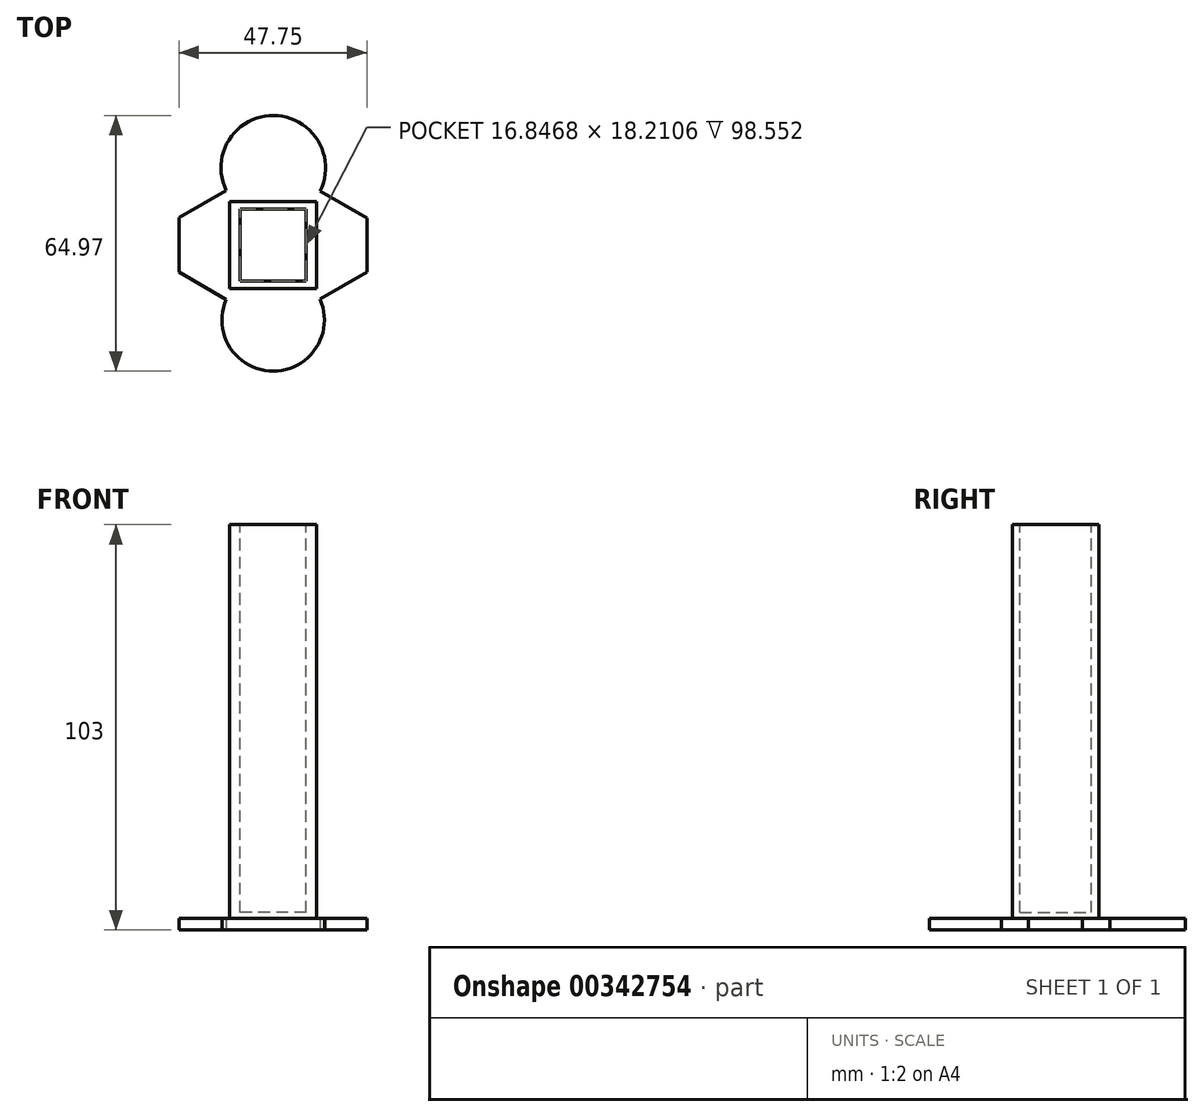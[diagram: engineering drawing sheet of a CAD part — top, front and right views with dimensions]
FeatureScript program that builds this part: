
annotation { "Feature Type Name" : "Feature", "Feature Type Description" : "" }
export const myFeature = defineFeature(function(context is Context, id is Id, definition is map)
    precondition{}
    {
        {
            var Q0;
            Q0=qCreatedBy(makeId("Top.planeOp"),FACE);
            var sketch = newSketch(context, id + "F0", { "sketchPlane" : qUnion([Q0])});
            skCircle(sketch, "E0.cCircle", {"center": v(0, 0) * mm, "radius": 10.33 * mm, "construction": true});
            skLineSegment(sketch, "E0.0", {"start": v(11.92, -0.02) * mm, "end": v(5.94, -10.34) * mm});
            skLineSegment(sketch, "E0.1", {"start": v(5.94, -10.34) * mm, "end": v(-5.98, -10.32) * mm});
            skLineSegment(sketch, "E0.2", {"start": v(-5.98, -10.32) * mm, "end": v(-11.92, 0.02) * mm});
            skLineSegment(sketch, "E0.3", {"start": v(-11.92, 0.02) * mm, "end": v(-5.94, 10.34) * mm});
            skLineSegment(sketch, "E0.4", {"start": v(-5.94, 10.34) * mm, "end": v(5.98, 10.32) * mm});
            skLineSegment(sketch, "E0.5", {"start": v(5.98, 10.32) * mm, "end": v(11.92, -0.02) * mm});
            skPoint(sketch, "E0.0.midPoint", {"position": v(8.93, -5.18) * mm});
            skCircle(sketch, "E1.cCircle", {"center": v(-11.92, 0.02) * mm, "radius": 12 * mm, "construction": true});
            skLineSegment(sketch, "E1.0", {"start": v(-23.93, -6.9) * mm, "end": v(-23.93, 6.95) * mm});
            skLineSegment(sketch, "E1.1", {"start": v(-23.93, 6.95) * mm, "end": v(-11.92, 13.88) * mm});
            skLineSegment(sketch, "E1.2", {"start": v(-11.92, 13.88) * mm, "end": v(0.08, 6.95) * mm});
            skLineSegment(sketch, "E1.3", {"start": v(0.08, 6.95) * mm, "end": v(0.08, -6.9) * mm});
            skLineSegment(sketch, "E1.4", {"start": v(0.08, -6.9) * mm, "end": v(-11.92, -13.84) * mm});
            skLineSegment(sketch, "E1.5", {"start": v(-11.92, -13.84) * mm, "end": v(-23.93, -6.9) * mm});
            skPoint(sketch, "E1.0.midPoint", {"position": v(-23.93, 0.02) * mm});
            skCircle(sketch, "E2.cCircle", {"center": v(11.92, -0.02) * mm, "radius": 11.9 * mm, "construction": true});
            skLineSegment(sketch, "E2.0", {"start": v(23.82, 6.85) * mm, "end": v(23.82, -6.9) * mm});
            skLineSegment(sketch, "E2.1", {"start": v(23.82, -6.9) * mm, "end": v(11.92, -13.76) * mm});
            skLineSegment(sketch, "E2.2", {"start": v(11.92, -13.76) * mm, "end": v(0.02, -6.9) * mm});
            skLineSegment(sketch, "E2.3", {"start": v(0.02, -6.9) * mm, "end": v(0.02, 6.85) * mm});
            skLineSegment(sketch, "E2.4", {"start": v(0.02, 6.85) * mm, "end": v(11.92, 13.72) * mm});
            skLineSegment(sketch, "E2.5", {"start": v(11.92, 13.72) * mm, "end": v(23.82, 6.85) * mm});
            skPoint(sketch, "E2.0.midPoint", {"position": v(23.82, -0.02) * mm});
            skCircle(sketch, "E3.cCircle", {"center": v(0.08, 6.95) * mm, "radius": 6.95 * mm, "construction": true});
            skLineSegment(sketch, "E3.0", {"start": v(4.01, -0.05) * mm, "end": v(-4.01, 0.05) * mm});
            skLineSegment(sketch, "E3.1", {"start": v(-4.01, 0.05) * mm, "end": v(-7.95, 7.04) * mm});
            skLineSegment(sketch, "E3.2", {"start": v(-7.95, 7.04) * mm, "end": v(-3.85, 13.95) * mm});
            skLineSegment(sketch, "E3.3", {"start": v(-3.85, 13.95) * mm, "end": v(4.17, 13.85) * mm});
            skLineSegment(sketch, "E3.4", {"start": v(4.17, 13.85) * mm, "end": v(8.1, 6.86) * mm});
            skLineSegment(sketch, "E3.5", {"start": v(8.1, 6.86) * mm, "end": v(4.01, -0.05) * mm});
            skCircle(sketch, "E4.cCircle", {"center": v(0.08, -6.9) * mm, "radius": 6.83 * mm, "construction": true});
            skLineSegment(sketch, "E4.0", {"start": v(4.02, -13.74) * mm, "end": v(-3.86, -13.74) * mm});
            skLineSegment(sketch, "E4.1", {"start": v(-3.86, -13.74) * mm, "end": v(-7.8, -6.9) * mm});
            skLineSegment(sketch, "E4.2", {"start": v(-7.8, -6.9) * mm, "end": v(-3.86, -0.08) * mm});
            skLineSegment(sketch, "E4.3", {"start": v(-3.86, -0.08) * mm, "end": v(4.02, -0.08) * mm});
            skLineSegment(sketch, "E4.4", {"start": v(4.02, -0.08) * mm, "end": v(7.96, -6.9) * mm});
            skLineSegment(sketch, "E4.5", {"start": v(7.96, -6.9) * mm, "end": v(4.02, -13.74) * mm});
            skPoint(sketch, "E4.0.midPoint", {"position": v(0.08, -13.74) * mm});
            skArc(sketch, "E5", {"start": v(-11.92, -13.84) * mm, "mid": v(0.06, -32.03) * mm, "end": v(11.92, -13.76) * mm});
            skArc(sketch, "E6", {"start": v(11.92, 13.72) * mm, "mid": v(0.13, 32.94) * mm, "end": v(-11.92, 13.88) * mm});
            skSolve(sketch);
        }
        {
            var Q0;
            {var subQ10=sQuery(id+"F0.wireOp",EDGE,"E3.3");Q0=makeQuery(id+"F0.imprint","IMPRINT",FACE,{"disambiguationData":[TD([[makeQuery(id+"F0.imprint","IMPRINT",EDGE,{"derivedFrom":subQ10}),-1.0]])]});}
            var Q1;
            {var subQ1=sQuery(id+"F0.wireOp",EDGE,"E0.2");Q1=makeQuery(id+"F0.imprint","IMPRINT",FACE,{"disambiguationData":[TD([[makeQuery(id+"F0.imprint","IMPRINT",EDGE,{"derivedFrom":subQ1}),-1.0]])]});}
            var Q2;
            {var subQ5=sQuery(id+"F0.wireOp",EDGE,"E0.4");var subQ6=sQuery(id+"F0.wireOp",EDGE,"E0.3");var subQ7=makeQuery(id+"F0.imprint","INTERSECT",VERTEX,{"derivedFrom":[subQ6,subQ5]});Q2=makeQuery(id+"F0.imprint","IMPRINT",FACE,{"disambiguationData":[TD([[makeQuery(id+"F0.imprint","IMPRINT",EDGE,{"disambiguationData":[TD([[subQ7,1.0]])],"derivedFrom":subQ6}),-1.0]])]});}
            var Q3;
            {var subQ0=sQuery(id+"F0.wireOp",EDGE,"E2.4");var subQ1=sQuery(id+"F0.wireOp",EDGE,"E0.5");var subQ2=makeQuery(id+"F0.imprint","INTERSECT",VERTEX,{"derivedFrom":[subQ1,subQ0]});Q3=makeQuery(id+"F0.imprint","IMPRINT",FACE,{"disambiguationData":[TD([[makeQuery(id+"F0.imprint","IMPRINT",EDGE,{"disambiguationData":[TD([[subQ2,-1.0]])],"derivedFrom":subQ1}),-1.0]])]});}
            var Q4;
            {var subQ5=sQuery(id+"F0.wireOp",EDGE,"E0.4");var subQ7=sQuery(id+"F0.wireOp",EDGE,"E0.5");var subQ8=makeQuery(id+"F0.imprint","INTERSECT",VERTEX,{"derivedFrom":[subQ5,subQ7]});Q4=makeQuery(id+"F0.imprint","IMPRINT",FACE,{"disambiguationData":[TD([[makeQuery(id+"F0.imprint","IMPRINT",EDGE,{"disambiguationData":[TD([[subQ8,1.0]])],"derivedFrom":subQ5}),-1.0]])]});}
            var Q5;
            {var subQ5=sQuery(id+"F0.wireOp",EDGE,"E0.5");var subQ9=sQuery(id+"F0.wireOp",EDGE,"E0.0");var subQ10=makeQuery(id+"F0.imprint","INTERSECT",VERTEX,{"derivedFrom":[subQ9,subQ5]});Q5=makeQuery(id+"F0.imprint","IMPRINT",FACE,{"disambiguationData":[TD([[makeQuery(id+"F0.imprint","IMPRINT",EDGE,{"disambiguationData":[TD([[subQ10,-1.0]])],"derivedFrom":subQ9}),-1.0]])]});}
            var Q6;
            {var subQ11=sQuery(id+"F0.wireOp",EDGE,"E4.0");Q6=makeQuery(id+"F0.imprint","IMPRINT",FACE,{"disambiguationData":[TD([[makeQuery(id+"F0.imprint","IMPRINT",EDGE,{"derivedFrom":subQ11}),-1.0]])]});}
            var Q7;
            {var subQ0=sQuery(id+"F0.wireOp",EDGE,"E0.1");var subQ1=sQuery(id+"F0.wireOp",EDGE,"E0.0");var subQ2=makeQuery(id+"F0.imprint","INTERSECT",VERTEX,{"derivedFrom":[subQ1,subQ0]});Q7=makeQuery(id+"F0.imprint","IMPRINT",FACE,{"disambiguationData":[TD([[makeQuery(id+"F0.imprint","IMPRINT",EDGE,{"disambiguationData":[TD([[subQ2,1.0]])],"derivedFrom":subQ1}),-1.0]])]});}
            var Q8;
            {var subQ9=sQuery(id+"F0.wireOp",EDGE,"E4.2");Q8=makeQuery(id+"F0.imprint","IMPRINT",FACE,{"disambiguationData":[TD([[makeQuery(id+"F0.imprint","IMPRINT",EDGE,{"derivedFrom":subQ9}),-1.0]])]});}
            var Q9;
            {var subQ5=sQuery(id+"F0.wireOp",EDGE,"E4.4");var subQ6=sQuery(id+"F0.wireOp",EDGE,"E0.0");var subQ7=makeQuery(id+"F0.imprint","INTERSECT",VERTEX,{"derivedFrom":[subQ6,subQ5]});Q9=makeQuery(id+"F0.imprint","IMPRINT",FACE,{"disambiguationData":[TD([[makeQuery(id+"F0.imprint","IMPRINT",EDGE,{"disambiguationData":[TD([[subQ7,-1.0]])],"derivedFrom":subQ6}),-1.0]])]});}
            var Q10;
            Q10=makeQuery(id+"F0.imprint","IMPRINT",FACE,{"disambiguationData":[TD([[makeQuery(id+"F0.imprint","IMPRINT",EDGE,{"derivedFrom":sQuery(id+"F0.wireOp",EDGE,"E2.0")}),-1.0]])]});
            var Q11;
            {var subQ0=sQuery(id+"F0.wireOp",EDGE,"E3.3");Q11=makeQuery(id+"F0.imprint","IMPRINT",FACE,{"disambiguationData":[TD([[makeQuery(id+"F0.imprint","IMPRINT",EDGE,{"derivedFrom":subQ0}),1.0]])]});}
            var Q12;
            {var subQ12=sQuery(id+"F0.wireOp",EDGE,"E0.2");Q12=makeQuery(id+"F0.imprint","IMPRINT",FACE,{"disambiguationData":[TD([[makeQuery(id+"F0.imprint","IMPRINT",EDGE,{"derivedFrom":subQ12}),1.0]])]});}
            var Q13;
            {var subQ0=sQuery(id+"F0.wireOp",EDGE,"E4.0");Q13=makeQuery(id+"F0.imprint","IMPRINT",FACE,{"disambiguationData":[TD([[makeQuery(id+"F0.imprint","IMPRINT",EDGE,{"derivedFrom":subQ0}),1.0]])]});}
            var Q14;
            {var subQ0=sQuery(id+"F0.wireOp",EDGE,"E2.4");var subQ1=sQuery(id+"F0.wireOp",EDGE,"E0.5");var subQ2=makeQuery(id+"F0.imprint","INTERSECT",VERTEX,{"derivedFrom":[subQ1,subQ0]});Q14=makeQuery(id+"F0.imprint","IMPRINT",FACE,{"disambiguationData":[TD([[makeQuery(id+"F0.imprint","IMPRINT",EDGE,{"disambiguationData":[TD([[subQ2,-1.0]])],"derivedFrom":subQ1}),1.0]])]});}
            var Q15;
            {var subQ0=sQuery(id+"F0.wireOp",EDGE,"E4.4");var subQ1=sQuery(id+"F0.wireOp",EDGE,"E0.0");var subQ2=makeQuery(id+"F0.imprint","INTERSECT",VERTEX,{"derivedFrom":[subQ1,subQ0]});Q15=makeQuery(id+"F0.imprint","IMPRINT",FACE,{"disambiguationData":[TD([[makeQuery(id+"F0.imprint","IMPRINT",EDGE,{"disambiguationData":[TD([[subQ2,-1.0]])],"derivedFrom":subQ1}),1.0]])]});}
            var Q16;
            {var subQ3=sQuery(id+"F0.wireOp",EDGE,"E0.3");var subQ6=sQuery(id+"F0.wireOp",EDGE,"E0.4");var subQ9=makeQuery(id+"F0.imprint","INTERSECT",VERTEX,{"derivedFrom":[subQ3,subQ6]});Q16=makeQuery(id+"F0.imprint","IMPRINT",FACE,{"disambiguationData":[TD([[makeQuery(id+"F0.imprint","IMPRINT",EDGE,{"disambiguationData":[TD([[subQ9,1.0]])],"derivedFrom":subQ3}),1.0]])]});}
            var Q17;
            {var subQ5=sQuery(id+"F0.wireOp",EDGE,"E1.4");var subQ6=sQuery(id+"F0.wireOp",EDGE,"E1.3");var subQ7=makeQuery(id+"F0.imprint","INTERSECT",VERTEX,{"derivedFrom":[subQ6,subQ5]});Q17=makeQuery(id+"F0.imprint","IMPRINT",FACE,{"disambiguationData":[TD([[makeQuery(id+"F0.imprint","IMPRINT",EDGE,{"disambiguationData":[TD([[subQ7,1.0]])],"derivedFrom":subQ6}),-1.0]])]});}
            var Q18;
            {var subQ0=sQuery(id+"F0.wireOp",EDGE,"E1.4");var subQ1=sQuery(id+"F0.wireOp",EDGE,"E0.1");var subQ2=makeQuery(id+"F0.imprint","INTERSECT",VERTEX,{"derivedFrom":[subQ1,subQ0]});Q18=makeQuery(id+"F0.imprint","IMPRINT",FACE,{"disambiguationData":[TD([[makeQuery(id+"F0.imprint","IMPRINT",EDGE,{"disambiguationData":[TD([[subQ2,-1.0]])],"derivedFrom":subQ1}),1.0]])]});}
            var Q19;
            {var subQ0=sQuery(id+"F0.wireOp",EDGE,"E2.4");var subQ1=sQuery(id+"F0.wireOp",EDGE,"E1.3");var subQ2=makeQuery(id+"F0.imprint","INTERSECT",VERTEX,{"derivedFrom":[subQ1,subQ0]});Q19=makeQuery(id+"F0.imprint","IMPRINT",FACE,{"disambiguationData":[TD([[makeQuery(id+"F0.imprint","IMPRINT",EDGE,{"disambiguationData":[TD([[subQ2,-1.0]])],"derivedFrom":subQ1}),-1.0]])]});}
            var Q20;
            {var subQ0=sQuery(id+"F0.wireOp",EDGE,"E3.0");var subQ1=sQuery(id+"F0.wireOp",EDGE,"E1.3");var subQ2=makeQuery(id+"F0.imprint","INTERSECT",VERTEX,{"derivedFrom":[subQ1,subQ0]});Q20=makeQuery(id+"F0.imprint","IMPRINT",FACE,{"disambiguationData":[TD([[makeQuery(id+"F0.imprint","IMPRINT",EDGE,{"disambiguationData":[TD([[subQ2,-1.0]])],"derivedFrom":subQ1}),-1.0]])]});}
            extrude(context, id + "F1", {"entities" : qUnion([Q0, Q1, Q2, Q3, Q4, Q5, Q6, Q7, Q8, Q9, Q10, Q11, Q12, Q13, Q14, Q15, Q16, Q17, Q18, Q19, Q20]), "depth" : 3 * mm});
        }
        {
            var Q0;
            Q0=makeQuery(id+"F1.opExtrude","CAP_FACE",FACE,{"disambiguationData":[OSD([sQuery(id+"F0.wireOp",EDGE,"E1.0"),sQuery(id+"F0.wireOp",EDGE,"E1.1"),sQuery(id+"F0.wireOp",EDGE,"E1.5"),sQuery(id+"F0.wireOp",EDGE,"E2.0"),sQuery(id+"F0.wireOp",EDGE,"E2.1"),sQuery(id+"F0.wireOp",EDGE,"E2.5"),sQuery(id+"F0.wireOp",EDGE,"E5"),sQuery(id+"F0.wireOp",EDGE,"E6")])],"isStart":false});
            var sketch = newSketch(context, id + "F2", { "sketchPlane" : qUnion([Q0])});
            skLineSegment(sketch, "E7.bottom", {"start": v(11.02, -11.04) * mm, "end": v(-11.02, -11.04) * mm});
            skLineSegment(sketch, "E7.top", {"start": v(11.02, 11.04) * mm, "end": v(-11.02, 11.04) * mm});
            skLineSegment(sketch, "E7.left", {"start": v(11.02, -11.04) * mm, "end": v(11.02, 11.04) * mm});
            skLineSegment(sketch, "E7.right", {"start": v(-11.02, -11.04) * mm, "end": v(-11.02, 11.04) * mm});
            skPoint(sketch, "E7.middle", {"position": v(0, 0) * mm});
            skSolve(sketch);
        }
        {
            var Q0;
            Q0 = qSketchRegion(id + "F2", true);
            extrude(context, id + "F3", {"entities" : qUnion([Q0]), "operationType" : NewBodyOperationType.ADD, "depth" : 100 * mm});
        }
        {
            var Q0;
            Q0=makeQuery(id+"F3.opExtrude","CAP_FACE",FACE,{"disambiguationData":[OSD([sQuery(id+"F2.wireOp",EDGE,"E7.bottom"),sQuery(id+"F2.wireOp",EDGE,"E7.top"),sQuery(id+"F2.wireOp",EDGE,"E7.left"),sQuery(id+"F2.wireOp",EDGE,"E7.right")])],"isStart":false});
            var sketch = newSketch(context, id + "F4", { "sketchPlane" : qUnion([Q0])});
            skLineSegment(sketch, "E8.bottom", {"start": v(8.42, -9.1) * mm, "end": v(-8.42, -9.1) * mm});
            skLineSegment(sketch, "E8.top", {"start": v(8.42, 9.1) * mm, "end": v(-8.42, 9.1) * mm});
            skLineSegment(sketch, "E8.left", {"start": v(8.42, -9.1) * mm, "end": v(8.42, 9.1) * mm});
            skLineSegment(sketch, "E8.right", {"start": v(-8.42, -9.1) * mm, "end": v(-8.42, 9.1) * mm});
            skPoint(sketch, "E8.middle", {"position": v(0, 0) * mm});
            skSolve(sketch);
        }
        {
            var Q0;
            Q0 = qSketchRegion(id + "F4", true);
            extrude(context, id + "F5", {"entities" : qUnion([Q0]), "operationType" : NewBodyOperationType.REMOVE, "oppositeDirection" : true, "depth" : 98.55 * mm});
        }
    });
